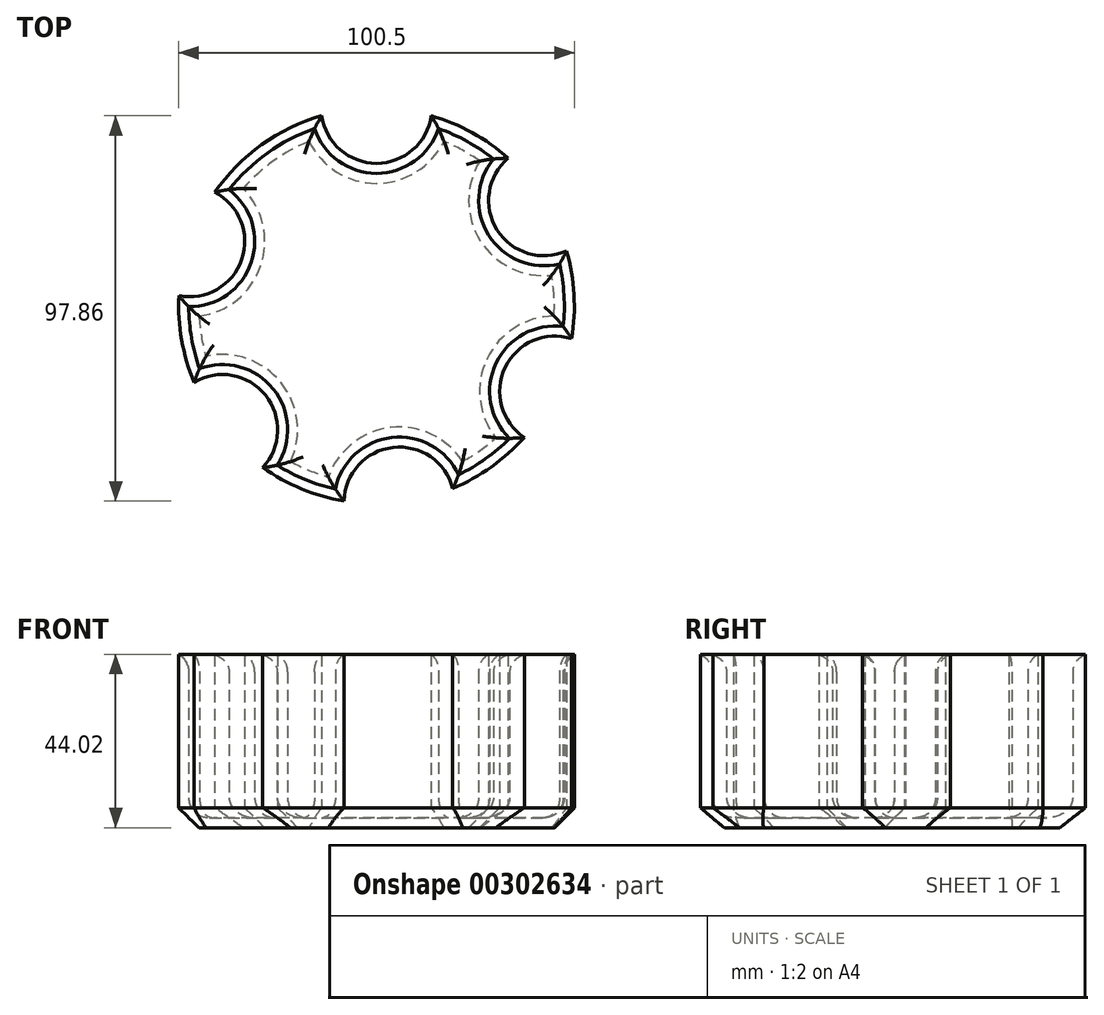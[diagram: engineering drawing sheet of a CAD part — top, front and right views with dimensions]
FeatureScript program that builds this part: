
annotation { "Feature Type Name" : "Feature", "Feature Type Description" : "" }
export const myFeature = defineFeature(function(context is Context, id is Id, definition is map)
    precondition{}
    {
        {
            var Q0;
            Q0=qCreatedBy(makeId("Top.planeOp"),FACE);
            var sketch = newSketch(context, id + "F0", { "sketchPlane" : qUnion([Q0])});
            skCircle(sketch, "E0", {"center": v(0, 0) * mm, "radius": 50.25 * mm});
            skCircle(sketch, "E1", {"center": v(0, 50.25) * mm, "radius": 14.04 * mm});
            skCircle(sketch, "E2.1.0", {"center": v(42.52, 26.78) * mm, "radius": 14.04 * mm});
            skCircle(sketch, "E2.2.0", {"center": v(45.32, -21.71) * mm, "radius": 14.04 * mm});
            skCircle(sketch, "E2.3.0", {"center": v(5.78, -49.92) * mm, "radius": 14.04 * mm});
            skCircle(sketch, "E2.4.0", {"center": v(-39.16, -31.49) * mm, "radius": 14.04 * mm});
            skLineSegment(sketch, "E2.anchor1", {"start": v(0, 0) * mm, "end": v(0, 50.25) * mm, "construction": true});
            skLineSegment(sketch, "E2.anchor2", {"start": v(0, 0) * mm, "end": v(-47.51, 16.36) * mm, "construction": true});
            skCircle(sketch, "E3.1.5.0", {"center": v(-47.51, 16.36) * mm, "radius": 14.04 * mm});
            skSolve(sketch);
        }
        {
            var Q0;
            {var subQ0=sQuery(id+"F0.wireOp",EDGE,"E2.1.0");var subQ1=sQuery(id+"F0.wireOp",EDGE,"E0");var subQ11=makeQuery(id+"F0.imprint","INTERSECT",VERTEX,{"disambiguationData":[OD(0.0)],"derivedFrom":[subQ1,subQ0]});Q0=makeQuery(id+"F0.imprint","IMPRINT",FACE,{"disambiguationData":[TD([[makeQuery(id+"F0.imprint","IMPRINT",EDGE,{"disambiguationData":[TD([[subQ11,-1.0]])],"derivedFrom":subQ1}),1.0]])]});}
            extrude(context, id + "F1", {"entities" : qUnion([Q0]), "depth" : 44.7 * mm});
        }
        {
            var Q0;
            Q0=makeQuery(id+"F1.opExtrude","CAP_FACE",FACE,{"disambiguationData":[OSD([sQuery(id+"F0.wireOp",EDGE,"E0"),sQuery(id+"F0.wireOp",EDGE,"E1"),sQuery(id+"F0.wireOp",EDGE,"E2.1.0"),sQuery(id+"F0.wireOp",EDGE,"E2.2.0"),sQuery(id+"F0.wireOp",EDGE,"E2.3.0"),sQuery(id+"F0.wireOp",EDGE,"E2.4.0"),sQuery(id+"F0.wireOp",EDGE,"E3.1.5.0")])],"isStart":false});
            shell(context, id + "F2", {"entities" : qUnion([Q0]), "thickness" : 2.54 * mm});
        }
        {
            var Q0;
            {var subQ0=sQuery(id+"F0.wireOp",EDGE,"E1");Q0=makeQuery(id+"F2.opShell","OFFSET_EDGE",EDGE,{"disambiguationData":[OSD([subQ0]),TDD([makeQuery(id+"F1.opExtrude","CAP_EDGE",EDGE,{"disambiguationData":[OSD([subQ0])],"isStart":true})])]});}
            var Q1;
            {var subQ0=sQuery(id+"F0.wireOp",EDGE,"E0");Q1=makeQuery(id+"F2.opShell","OFFSET_EDGE",EDGE,{"disambiguationData":[OSD([subQ0]),TDD([makeQuery(id+"F1.opExtrude","CAP_EDGE",EDGE,{"disambiguationData":[OSD([subQ0]),TDD([makeQuery(id+"F0.imprint","IMPRINT",EDGE,{"disambiguationData":[TD([[makeQuery(id+"F0.imprint","INTERSECT",VERTEX,{"disambiguationData":[OD(0.0)],"derivedFrom":[subQ0,sQuery(id+"F0.wireOp",EDGE,"E2.1.0")]}),-1.0]])],"derivedFrom":subQ0})])],"isStart":true})])]});}
            var Q2;
            {var subQ0=sQuery(id+"F0.wireOp",EDGE,"E2.1.0");Q2=makeQuery(id+"F2.opShell","OFFSET_EDGE",EDGE,{"disambiguationData":[OSD([subQ0]),TDD([makeQuery(id+"F1.opExtrude","CAP_EDGE",EDGE,{"disambiguationData":[OSD([subQ0])],"isStart":true})])]});}
            var Q3;
            {var subQ0=sQuery(id+"F0.wireOp",EDGE,"E0");Q3=makeQuery(id+"F2.opShell","OFFSET_EDGE",EDGE,{"disambiguationData":[OSD([subQ0]),TDD([makeQuery(id+"F1.opExtrude","CAP_EDGE",EDGE,{"disambiguationData":[OSD([subQ0]),TDD([makeQuery(id+"F0.imprint","IMPRINT",EDGE,{"disambiguationData":[TD([[makeQuery(id+"F0.imprint","INTERSECT",VERTEX,{"disambiguationData":[OD(1.0)],"derivedFrom":[subQ0,sQuery(id+"F0.wireOp",EDGE,"E2.1.0")]}),1.0]])],"derivedFrom":subQ0})])],"isStart":true})])]});}
            var Q4;
            {var subQ0=sQuery(id+"F0.wireOp",EDGE,"E2.2.0");Q4=makeQuery(id+"F2.opShell","OFFSET_EDGE",EDGE,{"disambiguationData":[OSD([subQ0]),TDD([makeQuery(id+"F1.opExtrude","CAP_EDGE",EDGE,{"disambiguationData":[OSD([subQ0])],"isStart":true})])]});}
            var Q5;
            {var subQ0=sQuery(id+"F0.wireOp",EDGE,"E0");Q5=makeQuery(id+"F2.opShell","OFFSET_EDGE",EDGE,{"disambiguationData":[OSD([subQ0]),TDD([makeQuery(id+"F1.opExtrude","CAP_EDGE",EDGE,{"disambiguationData":[OSD([subQ0]),TDD([makeQuery(id+"F0.imprint","IMPRINT",EDGE,{"disambiguationData":[TD([[makeQuery(id+"F0.imprint","INTERSECT",VERTEX,{"disambiguationData":[OD(1.0)],"derivedFrom":[subQ0,sQuery(id+"F0.wireOp",EDGE,"E2.3.0")]}),-1.0]])],"derivedFrom":subQ0})])],"isStart":true})])]});}
            var Q6;
            {var subQ0=sQuery(id+"F0.wireOp",EDGE,"E0");Q6=makeQuery(id+"F2.opShell","OFFSET_EDGE",EDGE,{"disambiguationData":[OSD([subQ0]),TDD([makeQuery(id+"F1.opExtrude","CAP_EDGE",EDGE,{"disambiguationData":[OSD([subQ0]),TDD([makeQuery(id+"F0.imprint","IMPRINT",EDGE,{"disambiguationData":[TD([[makeQuery(id+"F0.imprint","INTERSECT",VERTEX,{"disambiguationData":[OD(1.0)],"derivedFrom":[subQ0,sQuery(id+"F0.wireOp",EDGE,"E1")]}),-1.0]])],"derivedFrom":subQ0})])],"isStart":true})])]});}
            var Q7;
            {var subQ0=sQuery(id+"F0.wireOp",EDGE,"E3.1.5.0");Q7=makeQuery(id+"F2.opShell","OFFSET_EDGE",EDGE,{"disambiguationData":[OSD([subQ0]),TDD([makeQuery(id+"F1.opExtrude","CAP_EDGE",EDGE,{"disambiguationData":[OSD([subQ0])],"isStart":true})])]});}
            var Q8;
            {var subQ0=sQuery(id+"F0.wireOp",EDGE,"E0");Q8=makeQuery(id+"F2.opShell","OFFSET_EDGE",EDGE,{"disambiguationData":[OSD([subQ0]),TDD([makeQuery(id+"F1.opExtrude","CAP_EDGE",EDGE,{"disambiguationData":[OSD([subQ0]),TDD([makeQuery(id+"F0.imprint","IMPRINT",EDGE,{"disambiguationData":[TD([[makeQuery(id+"F0.imprint","INTERSECT",VERTEX,{"disambiguationData":[OD(1.0)],"derivedFrom":[subQ0,sQuery(id+"F0.wireOp",EDGE,"E3.1.5.0")]}),-1.0]])],"derivedFrom":subQ0})])],"isStart":true})])]});}
            var Q9;
            {var subQ0=sQuery(id+"F0.wireOp",EDGE,"E2.4.0");Q9=makeQuery(id+"F2.opShell","OFFSET_EDGE",EDGE,{"disambiguationData":[OSD([subQ0]),TDD([makeQuery(id+"F1.opExtrude","CAP_EDGE",EDGE,{"disambiguationData":[OSD([subQ0])],"isStart":true})])]});}
            var Q10;
            {var subQ0=sQuery(id+"F0.wireOp",EDGE,"E0");Q10=makeQuery(id+"F2.opShell","OFFSET_EDGE",EDGE,{"disambiguationData":[OSD([subQ0]),TDD([makeQuery(id+"F1.opExtrude","CAP_EDGE",EDGE,{"disambiguationData":[OSD([subQ0]),TDD([makeQuery(id+"F0.imprint","IMPRINT",EDGE,{"disambiguationData":[TD([[makeQuery(id+"F0.imprint","INTERSECT",VERTEX,{"disambiguationData":[OD(1.0)],"derivedFrom":[subQ0,sQuery(id+"F0.wireOp",EDGE,"E2.4.0")]}),-1.0]])],"derivedFrom":subQ0})])],"isStart":true})])]});}
            var Q11;
            {var subQ0=sQuery(id+"F0.wireOp",EDGE,"E2.3.0");Q11=makeQuery(id+"F2.opShell","OFFSET_EDGE",EDGE,{"disambiguationData":[OSD([subQ0]),TDD([makeQuery(id+"F1.opExtrude","CAP_EDGE",EDGE,{"disambiguationData":[OSD([subQ0])],"isStart":true})])]});}
            fillet(context, id + "F3", {"entities" : qUnion([Q0, Q1, Q2, Q3, Q4, Q5, Q6, Q7, Q8, Q9, Q10, Q11]), "radius" : 5.08 * mm, "tangentPropagation" : true, "allowEdgeOverflow" : false});
        }
        {
            var Q0;
            Q0=makeQuery(id+"F1.opExtrude","CAP_FACE",FACE,{"disambiguationData":[OSD([sQuery(id+"F0.wireOp",EDGE,"E0"),sQuery(id+"F0.wireOp",EDGE,"E1"),sQuery(id+"F0.wireOp",EDGE,"E2.1.0"),sQuery(id+"F0.wireOp",EDGE,"E2.2.0"),sQuery(id+"F0.wireOp",EDGE,"E2.3.0"),sQuery(id+"F0.wireOp",EDGE,"E2.4.0"),sQuery(id+"F0.wireOp",EDGE,"E3.1.5.0")])],"isStart":true});
            chamfer(context, id + "F4", {"entities" : qUnion([Q0]), "width" : 5.08 * mm, "tangentPropagation" : true});
        }
        {
            var Q0;
            {var subQ0=sQuery(id+"F0.wireOp",EDGE,"E1");Q0=makeQuery(id+"F2.opShell","OFFSET_EDGE",EDGE,{"disambiguationData":[OSD([subQ0]),TDD([makeQuery(id+"F1.opExtrude","CAP_EDGE",EDGE,{"disambiguationData":[OSD([subQ0])],"isStart":false})])]});}
            var Q1;
            {var subQ0=sQuery(id+"F0.wireOp",EDGE,"E0");Q1=makeQuery(id+"F2.opShell","OFFSET_EDGE",EDGE,{"disambiguationData":[OSD([subQ0]),TDD([makeQuery(id+"F1.opExtrude","CAP_EDGE",EDGE,{"disambiguationData":[OSD([subQ0]),TDD([makeQuery(id+"F0.imprint","IMPRINT",EDGE,{"disambiguationData":[TD([[makeQuery(id+"F0.imprint","INTERSECT",VERTEX,{"disambiguationData":[OD(0.0)],"derivedFrom":[subQ0,sQuery(id+"F0.wireOp",EDGE,"E2.1.0")]}),-1.0]])],"derivedFrom":subQ0})])],"isStart":false})])]});}
            var Q2;
            {var subQ0=sQuery(id+"F0.wireOp",EDGE,"E2.1.0");Q2=makeQuery(id+"F2.opShell","OFFSET_EDGE",EDGE,{"disambiguationData":[OSD([subQ0]),TDD([makeQuery(id+"F1.opExtrude","CAP_EDGE",EDGE,{"disambiguationData":[OSD([subQ0])],"isStart":false})])]});}
            var Q3;
            {var subQ0=sQuery(id+"F0.wireOp",EDGE,"E0");Q3=makeQuery(id+"F2.opShell","OFFSET_EDGE",EDGE,{"disambiguationData":[OSD([subQ0]),TDD([makeQuery(id+"F1.opExtrude","CAP_EDGE",EDGE,{"disambiguationData":[OSD([subQ0]),TDD([makeQuery(id+"F0.imprint","IMPRINT",EDGE,{"disambiguationData":[TD([[makeQuery(id+"F0.imprint","INTERSECT",VERTEX,{"disambiguationData":[OD(1.0)],"derivedFrom":[subQ0,sQuery(id+"F0.wireOp",EDGE,"E2.1.0")]}),1.0]])],"derivedFrom":subQ0})])],"isStart":false})])]});}
            var Q4;
            {var subQ0=sQuery(id+"F0.wireOp",EDGE,"E2.2.0");Q4=makeQuery(id+"F2.opShell","OFFSET_EDGE",EDGE,{"disambiguationData":[OSD([subQ0]),TDD([makeQuery(id+"F1.opExtrude","CAP_EDGE",EDGE,{"disambiguationData":[OSD([subQ0])],"isStart":false})])]});}
            var Q5;
            {var subQ0=sQuery(id+"F0.wireOp",EDGE,"E0");Q5=makeQuery(id+"F2.opShell","OFFSET_EDGE",EDGE,{"disambiguationData":[OSD([subQ0]),TDD([makeQuery(id+"F1.opExtrude","CAP_EDGE",EDGE,{"disambiguationData":[OSD([subQ0]),TDD([makeQuery(id+"F0.imprint","IMPRINT",EDGE,{"disambiguationData":[TD([[makeQuery(id+"F0.imprint","INTERSECT",VERTEX,{"disambiguationData":[OD(1.0)],"derivedFrom":[subQ0,sQuery(id+"F0.wireOp",EDGE,"E2.3.0")]}),-1.0]])],"derivedFrom":subQ0})])],"isStart":false})])]});}
            var Q6;
            {var subQ0=sQuery(id+"F0.wireOp",EDGE,"E2.3.0");Q6=makeQuery(id+"F2.opShell","OFFSET_EDGE",EDGE,{"disambiguationData":[OSD([subQ0]),TDD([makeQuery(id+"F1.opExtrude","CAP_EDGE",EDGE,{"disambiguationData":[OSD([subQ0])],"isStart":false})])]});}
            var Q7;
            {var subQ0=sQuery(id+"F0.wireOp",EDGE,"E0");Q7=makeQuery(id+"F2.opShell","OFFSET_EDGE",EDGE,{"disambiguationData":[OSD([subQ0]),TDD([makeQuery(id+"F1.opExtrude","CAP_EDGE",EDGE,{"disambiguationData":[OSD([subQ0]),TDD([makeQuery(id+"F0.imprint","IMPRINT",EDGE,{"disambiguationData":[TD([[makeQuery(id+"F0.imprint","INTERSECT",VERTEX,{"disambiguationData":[OD(1.0)],"derivedFrom":[subQ0,sQuery(id+"F0.wireOp",EDGE,"E2.4.0")]}),-1.0]])],"derivedFrom":subQ0})])],"isStart":false})])]});}
            var Q8;
            {var subQ0=sQuery(id+"F0.wireOp",EDGE,"E2.4.0");Q8=makeQuery(id+"F2.opShell","OFFSET_EDGE",EDGE,{"disambiguationData":[OSD([subQ0]),TDD([makeQuery(id+"F1.opExtrude","CAP_EDGE",EDGE,{"disambiguationData":[OSD([subQ0])],"isStart":false})])]});}
            var Q9;
            {var subQ0=sQuery(id+"F0.wireOp",EDGE,"E0");Q9=makeQuery(id+"F2.opShell","OFFSET_EDGE",EDGE,{"disambiguationData":[OSD([subQ0]),TDD([makeQuery(id+"F1.opExtrude","CAP_EDGE",EDGE,{"disambiguationData":[OSD([subQ0]),TDD([makeQuery(id+"F0.imprint","IMPRINT",EDGE,{"disambiguationData":[TD([[makeQuery(id+"F0.imprint","INTERSECT",VERTEX,{"disambiguationData":[OD(1.0)],"derivedFrom":[subQ0,sQuery(id+"F0.wireOp",EDGE,"E3.1.5.0")]}),-1.0]])],"derivedFrom":subQ0})])],"isStart":false})])]});}
            var Q10;
            {var subQ0=sQuery(id+"F0.wireOp",EDGE,"E3.1.5.0");Q10=makeQuery(id+"F2.opShell","OFFSET_EDGE",EDGE,{"disambiguationData":[OSD([subQ0]),TDD([makeQuery(id+"F1.opExtrude","CAP_EDGE",EDGE,{"disambiguationData":[OSD([subQ0])],"isStart":false})])]});}
            var Q11;
            {var subQ0=sQuery(id+"F0.wireOp",EDGE,"E0");Q11=makeQuery(id+"F2.opShell","OFFSET_EDGE",EDGE,{"disambiguationData":[OSD([subQ0]),TDD([makeQuery(id+"F1.opExtrude","CAP_EDGE",EDGE,{"disambiguationData":[OSD([subQ0]),TDD([makeQuery(id+"F0.imprint","IMPRINT",EDGE,{"disambiguationData":[TD([[makeQuery(id+"F0.imprint","INTERSECT",VERTEX,{"disambiguationData":[OD(1.0)],"derivedFrom":[subQ0,sQuery(id+"F0.wireOp",EDGE,"E1")]}),-1.0]])],"derivedFrom":subQ0})])],"isStart":false})])]});}
            fillet(context, id + "F5", {"entities" : qUnion([Q0, Q1, Q2, Q3, Q4, Q5, Q6, Q7, Q8, Q9, Q10, Q11]), "radius" : 5.08 * mm, "tangentPropagation" : true, "allowEdgeOverflow" : false});
        }
    });
